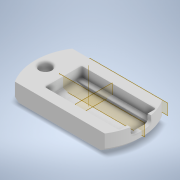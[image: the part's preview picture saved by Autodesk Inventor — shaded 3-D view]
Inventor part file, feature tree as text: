
AUTODESK INVENTOR PART (.ipt)
format: ipt  version: 2021 (Build 250183000, 183)  size: 673,792 bytes
history: native  units: in
note: dims shown in document units (in); Inventor stores cm internally (conversion verified against a paired STEP export)
features: extrude x8, sketch x8, plane x3, fillet x3, chamfer x2, other x1, pattern_circular x1, mirror x1
ambient origin geometry x8: Origin, YZ Plane, XZ Plane, XY Plane, X Axis, Y Axis, Z Axis, Center Point
bodies: Solid1 (feature_tree)
feature tree (27):
  extrude  "Extrusion1"  Depth=0.315in TaperAngle=0.0deg
  chamfer  "Chamfer2"  Distance=0.189in
  extrude  "Extrusion2"  Depth=0.1575in
  extrude  "Extrusion3"  Depth=0.2205in
  other  "Work Axis1"
  plane  "Work Plane1"
  extrude  "Extrusion5"  Depth=0.0315in
  extrude  "Extrusion4"  Depth=0.0315in
  fillet  "Fillet4"  Radius=0.5in
  pattern_circular  "Circular Pattern2"  [2 undecoded]
  chamfer  "Chamfer3"  Distance=0.25in
  fillet  "Fillet7"  [1 undecoded]
  extrude  "Extrusion9"  Depth=0.0315in TaperAngle=0.0deg
  extrude  "Extrusion10"  Depth=0.0315in
  fillet  "Fillet9"  Radius=0.0394in
  plane  "Work Plane3"
  extrude  "Extrusion11"  TaperAngle=45.0deg  [1 undecoded]
  mirror  "Mirror5"
  plane  "Work Plane4"
  sketch  "Sketch1"  dims[d0=2.0472in d3=0.315in d4=0.0in]
  sketch  "Sketch2"  dims[d5=1.4315in]
  sketch  "Sketch3"  dims[d6=0.7079in]
  sketch  "Sketch4"  dims[d7=0.3539in]
  sketch  "Sketch7"  dims[d8=0.4882in d9=0.189in d10=0.0in]
  sketch  "Sketch12"  dims[d11=0.0in d14=0.1575in]
  sketch  "Sketch13"  dims[d15=0.0in d16=0.0in d17=0.2205in]
  sketch  "Sketch15"  dims[d18=0.2047in d19=0.0in d23=0.8268in d24=0.3539in d28=0.5in d29=1.4in d30=0.25in d31=0.0in d32=0.063in d33=0.0in d44=0.1575in d47=0.0394in d48=0.0in d49=0.0in d51=0.0in d54=0.063in d55=0.0in d56=45.0deg d58=0.0394in d59=0.1181in d60=1.9685in d61=240.0deg d63=0.0591in d64=0.1969in d65=45.0deg d72=0.0315in d79=0.1039in d80=0.9517in d81=0.4759in d82=0.9728in d83=0.4864in d84=0.0394in d85=0.0in d86=0.547in d87=0.2735in d88=0.0787in d89=0.0in d90=0.0787in d92=-0.1969in d93=0.5906in d94=0.0in d95=0.5906in d91=0.0197in]
note: 4 required parameter values undecoded (feature->parameter linkage not recoverable at this tier; creation-order binding heuristic only, values carry confidence <= 0.55)
